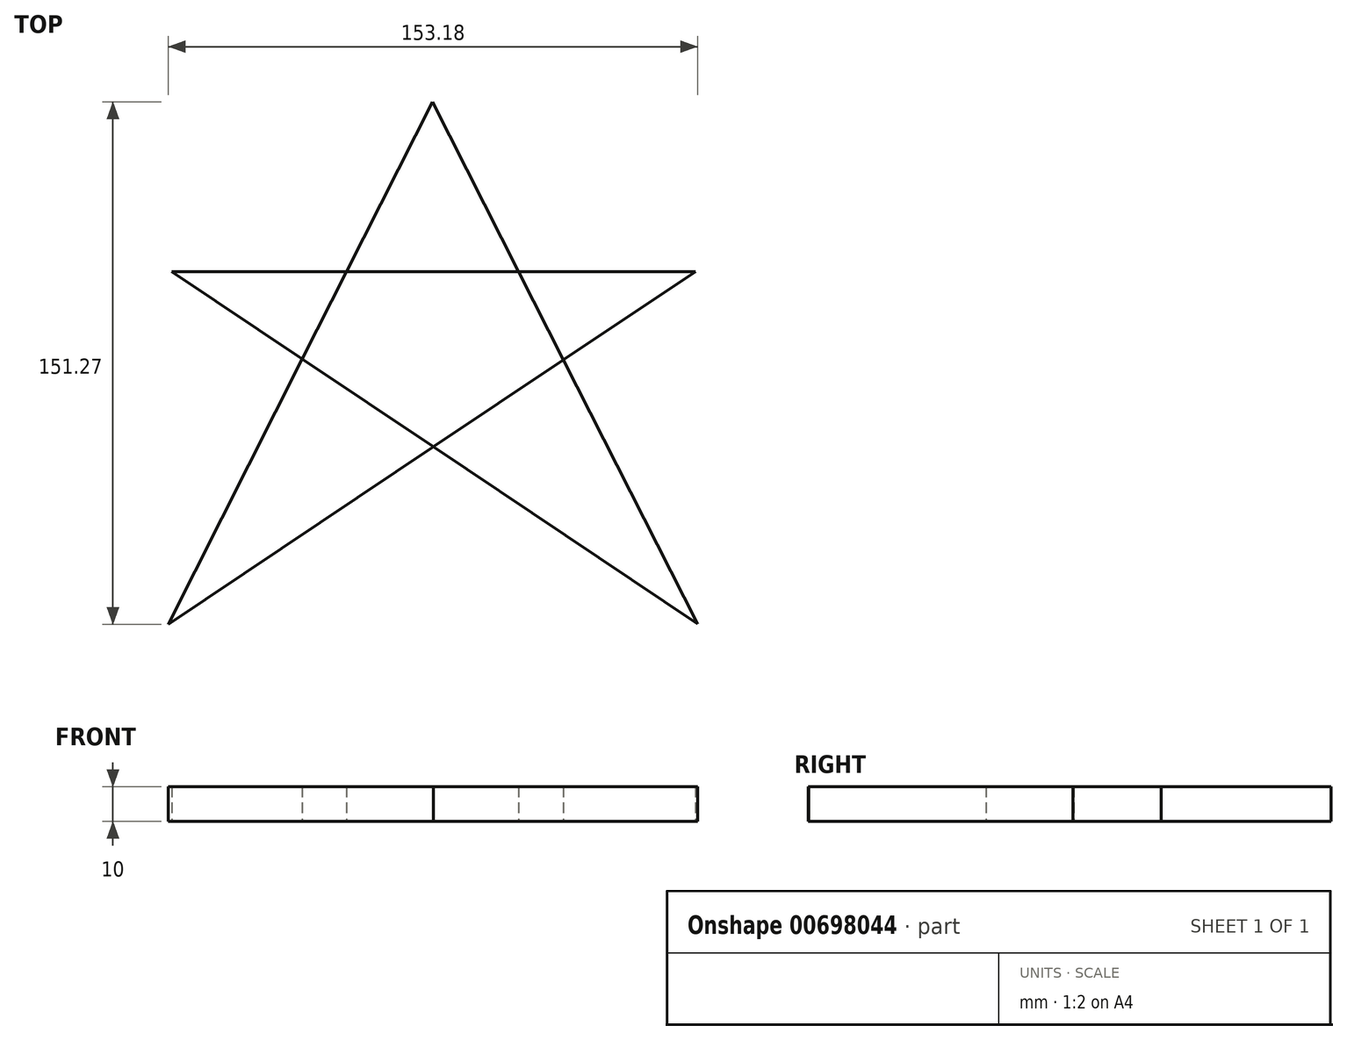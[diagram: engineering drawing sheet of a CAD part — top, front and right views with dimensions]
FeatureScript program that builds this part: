
annotation { "Feature Type Name" : "Feature", "Feature Type Description" : "" }
export const myFeature = defineFeature(function(context is Context, id is Id, definition is map)
    precondition{}
    {
        {
            var Q0;
            Q0=qCreatedBy(makeId("Top.planeOp"),FACE);
            var sketch = newSketch(context, id + "F0", { "sketchPlane" : qUnion([Q0])});
            skLineSegment(sketch, "E0", {"start": v(-75.38, 25.64) * mm, "end": v(76.07, 25.64) * mm});
            skLineSegment(sketch, "E1", {"start": v(76.07, 25.64) * mm, "end": v(-76.42, -76.48) * mm});
            skLineSegment(sketch, "E2", {"start": v(-76.42, -76.48) * mm, "end": v(0, 74.8) * mm});
            skLineSegment(sketch, "E3", {"start": v(0, 74.8) * mm, "end": v(76.76, -76.3) * mm});
            skLineSegment(sketch, "E4", {"start": v(76.76, -76.3) * mm, "end": v(-75.38, 25.64) * mm});
            skSolve(sketch);
        }
        {
            var Q0;
            {var subQ0=sQuery(id+"F0.wireOp",EDGE,"E3");var subQ1=sQuery(id+"F0.wireOp",EDGE,"E1");var subQ2=makeQuery(id+"F0.imprint","INTERSECT",VERTEX,{"derivedFrom":[subQ1,subQ0]});Q0=makeQuery(id+"F0.imprint","IMPRINT",FACE,{"disambiguationData":[TD([[makeQuery(id+"F0.imprint","IMPRINT",EDGE,{"disambiguationData":[TD([[subQ2,-1.0]])],"derivedFrom":subQ1}),1.0]])]});}
            var Q1;
            {var subQ0=sQuery(id+"F0.wireOp",EDGE,"E2");var subQ1=sQuery(id+"F0.wireOp",EDGE,"E1");var subQ2=makeQuery(id+"F0.imprint","INTERSECT",VERTEX,{"derivedFrom":[subQ1,subQ0]});Q1=makeQuery(id+"F0.imprint","IMPRINT",FACE,{"disambiguationData":[TD([[makeQuery(id+"F0.imprint","IMPRINT",EDGE,{"disambiguationData":[TD([[subQ2,1.0]])],"derivedFrom":subQ1}),-1.0]])]});}
            var Q2;
            {var subQ0=sQuery(id+"F0.wireOp",EDGE,"E4");var subQ1=sQuery(id+"F0.wireOp",EDGE,"E0");var subQ2=makeQuery(id+"F0.imprint","INTERSECT",VERTEX,{"derivedFrom":[subQ1,subQ0]});Q2=makeQuery(id+"F0.imprint","IMPRINT",FACE,{"disambiguationData":[TD([[makeQuery(id+"F0.imprint","IMPRINT",EDGE,{"disambiguationData":[TD([[subQ2,-1.0]])],"derivedFrom":subQ1}),-1.0]])]});}
            var Q3;
            {var subQ0=sQuery(id+"F0.wireOp",EDGE,"E2");var subQ1=sQuery(id+"F0.wireOp",EDGE,"E0");var subQ2=makeQuery(id+"F0.imprint","INTERSECT",VERTEX,{"derivedFrom":[subQ1,subQ0]});Q3=makeQuery(id+"F0.imprint","IMPRINT",FACE,{"disambiguationData":[TD([[makeQuery(id+"F0.imprint","IMPRINT",EDGE,{"disambiguationData":[TD([[subQ2,-1.0]])],"derivedFrom":subQ1}),1.0]])]});}
            var Q4;
            {var subQ0=sQuery(id+"F0.wireOp",EDGE,"E1");var subQ1=sQuery(id+"F0.wireOp",EDGE,"E0");var subQ2=makeQuery(id+"F0.imprint","INTERSECT",VERTEX,{"derivedFrom":[subQ1,subQ0]});Q4=makeQuery(id+"F0.imprint","IMPRINT",FACE,{"disambiguationData":[TD([[makeQuery(id+"F0.imprint","IMPRINT",EDGE,{"disambiguationData":[TD([[subQ2,1.0]])],"derivedFrom":subQ1}),-1.0]])]});}
            extrude(context, id + "F1", {"entities" : qUnion([Q0, Q1, Q2, Q3, Q4]), "depth" : 10 * mm, "offsetDistance" : 25.4 * mm});
        }
    });
